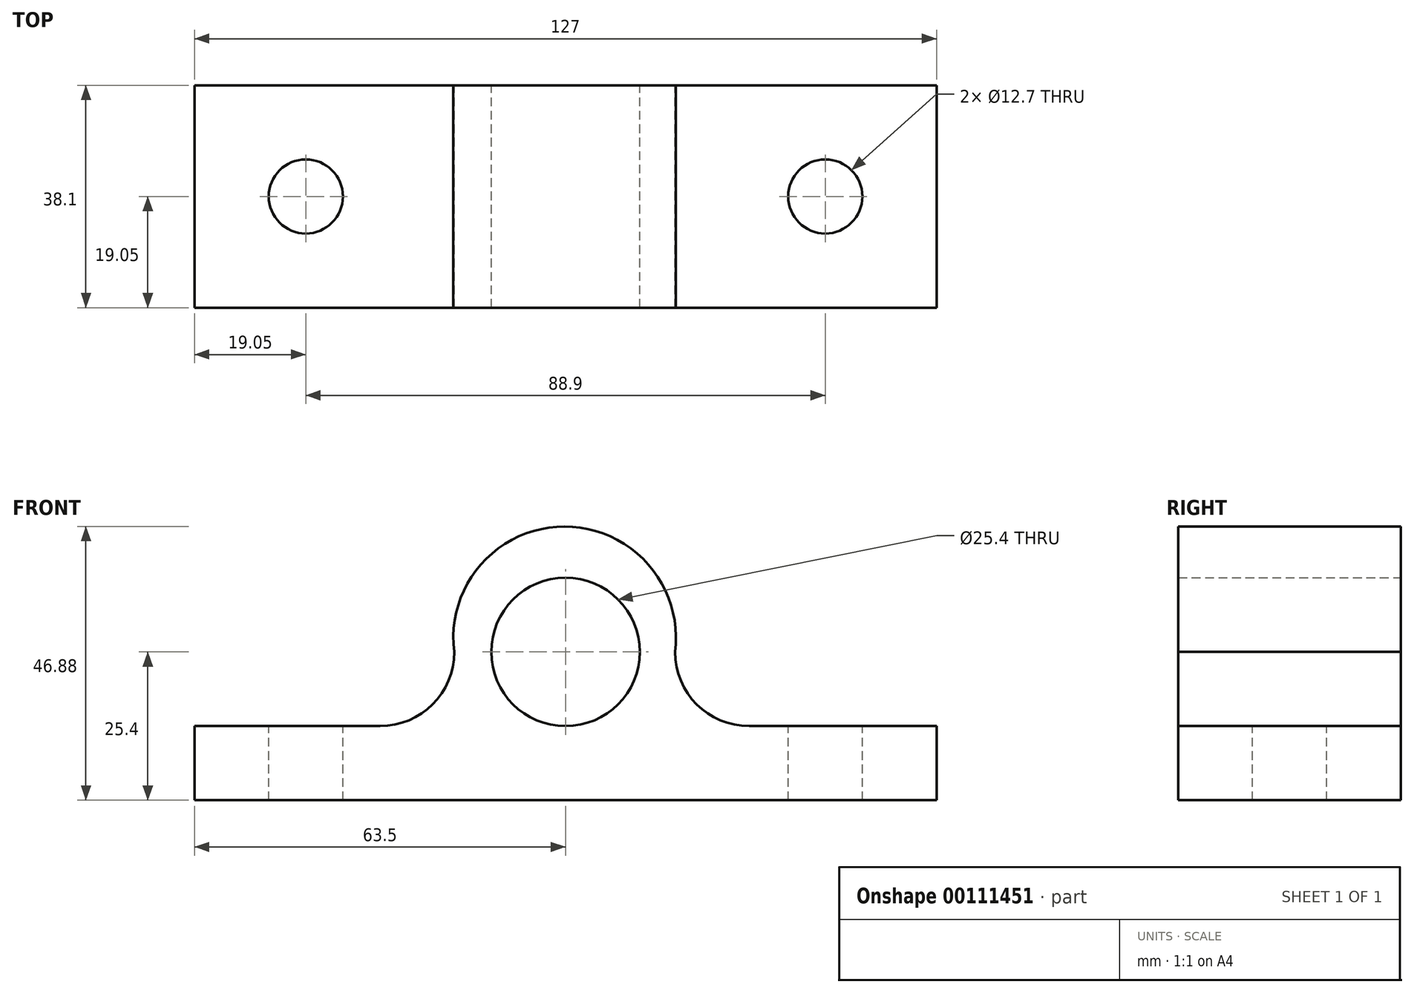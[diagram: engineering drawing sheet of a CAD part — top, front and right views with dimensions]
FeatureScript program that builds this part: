
annotation { "Feature Type Name" : "Feature", "Feature Type Description" : "" }
export const myFeature = defineFeature(function(context is Context, id is Id, definition is map)
    precondition{}
    {
        {
            var Q0;
            Q0=qCreatedBy(makeId("Front.planeOp"),FACE);
            var sketch = newSketch(context, id + "F0", { "sketchPlane" : qUnion([Q0])});
            skLineSegment(sketch, "E0.bottom", {"start": v(-63.5, 0) * mm, "end": v(63.5, 0) * mm});
            skLineSegment(sketch, "E0.top", {"start": v(-63.5, 12.7) * mm, "end": v(-37.54, 12.7) * mm});
            skLineSegment(sketch, "E0.left", {"start": v(-63.5, 0) * mm, "end": v(-63.5, 12.7) * mm});
            skLineSegment(sketch, "E0.right", {"start": v(63.5, 0) * mm, "end": v(63.5, 12.7) * mm});
            skLineSegment(sketch, "E1.trimOffspring", {"start": v(37.54, 12.7) * mm, "end": v(63.5, 12.7) * mm});
            skLineSegment(sketch, "E2", {"start": v(0, 12.7) * mm, "end": v(19.05, 12.7) * mm, "construction": true});
            skLineSegment(sketch, "E3", {"start": v(0, 12.7) * mm, "end": v(-19.05, 12.7) * mm, "construction": true});
            skLineSegment(sketch, "E4", {"start": v(31.44, 12.7) * mm, "end": v(37.54, 12.7) * mm});
            skLineSegment(sketch, "E5", {"start": v(-31.75, 12.7) * mm, "end": v(-37.54, 12.7) * mm});
            skPoint(sketch, "E6.visualSharp", {"position": v(-19.05, 12.7) * mm});
            skArc(sketch, "E6.filletArc", {"start": v(-31.75, 12.7) * mm, "mid": v(-22.77, 16.42) * mm, "end": v(-19.05, 25.4) * mm});
            skPoint(sketch, "E7.visualSharp", {"position": v(19.05, 12.7) * mm});
            skArc(sketch, "E7.filletArc", {"start": v(18.74, 25.4) * mm, "mid": v(22.46, 16.42) * mm, "end": v(31.44, 12.7) * mm});
            skLineSegment(sketch, "E8", {"start": v(0, 0) * mm, "end": v(0, 25.4) * mm});
            skCircle(sketch, "E9", {"center": v(0, 25.4) * mm, "radius": 12.7 * mm});
            skArc(sketch, "E10", {"start": v(18.74, 25.4) * mm, "mid": v(-0.16, 46.88) * mm, "end": v(-19.05, 25.4) * mm});
            skSolve(sketch);
        }
        {
            var Q0;
            Q0 = qSketchRegion(id + "F0", true);
            extrude(context, id + "F1", {"entities" : qUnion([Q0]), "depth" : 38.1 * mm});
        }
        {
            var Q0;
            Q0=makeQuery(id+"F1.opExtrude","SWEPT_FACE",FACE,{"disambiguationData":[OSD([sQuery(id+"F0.wireOp",EDGE,"E1.trimOffspring"),sQuery(id+"F0.wireOp",EDGE,"E4")])]});
            var sketch = newSketch(context, id + "F2", { "sketchPlane" : qUnion([Q0])});
            skPoint(sketch, "E11.endSnap0", {"position": v(47.47, 0) * mm});
            skCircle(sketch, "E12", {"center": v(44.45, -19.05) * mm, "radius": 6.35 * mm});
            skCircle(sketch, "E13", {"center": v(-44.45, -19.05) * mm, "radius": 6.35 * mm});
            skSolve(sketch);
        }
        {
            var Q0;
            Q0=makeQuery(id+"F2.imprint","IMPRINT",FACE,{"disambiguationData":[TD([[makeQuery(id+"F2.imprint","IMPRINT",EDGE,{"derivedFrom":sQuery(id+"F2.wireOp",EDGE,"E13")}),1.0]])]});
            var Q1;
            Q1=makeQuery(id+"F1.opExtrude","SWEPT_FACE",FACE,{"disambiguationData":[OSD([sQuery(id+"F0.wireOp",EDGE,"E0.bottom")])]});
            extrude(context, id + "F3", {"entities" : qUnion([Q0]), "operationType" : NewBodyOperationType.REMOVE, "endBound" : BoundingType.UP_TO_SURFACE, "oppositeDirection" : true, "endBoundEntityFace" : qUnion([Q1]), "depth" : 25.4 * mm});
        }
        {
            var Q0;
            Q0 = qSketchRegion(id + "F2", true);
            var Q1;
            Q1=makeQuery(id+"F1.opExtrude","SWEPT_FACE",FACE,{"disambiguationData":[OSD([sQuery(id+"F0.wireOp",EDGE,"E0.bottom")])]});
            extrude(context, id + "F4", {"entities" : qUnion([Q0]), "operationType" : NewBodyOperationType.REMOVE, "endBound" : BoundingType.UP_TO_SURFACE, "oppositeDirection" : true, "endBoundEntityFace" : qUnion([Q1]), "depth" : 25.4 * mm});
        }
    });
